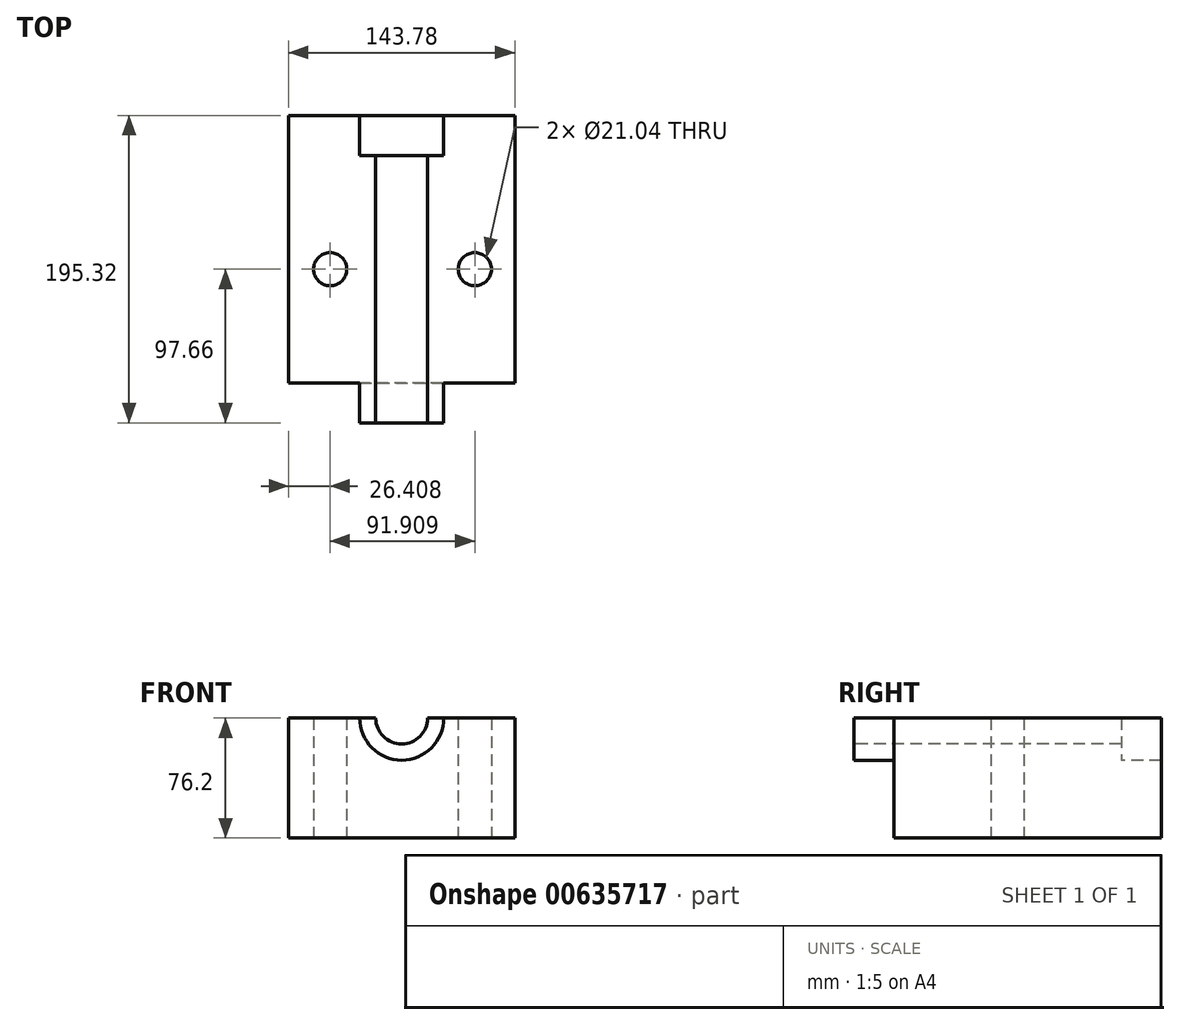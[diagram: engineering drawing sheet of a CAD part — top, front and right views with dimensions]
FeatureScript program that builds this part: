
annotation { "Feature Type Name" : "Feature", "Feature Type Description" : "" }
export const myFeature = defineFeature(function(context is Context, id is Id, definition is map)
    precondition{}
    {
        {
            var Q0;
            Q0=qCreatedBy(makeId("Top.planeOp"),FACE);
            var sketch = newSketch(context, id + "F0", { "sketchPlane" : qUnion([Q0])});
            skLineSegment(sketch, "E0.bottom", {"start": v(71.9, -72.26) * mm, "end": v(-71.9, -72.26) * mm});
            skLineSegment(sketch, "E0.top", {"start": v(71.9, 72.26) * mm, "end": v(-71.9, 72.26) * mm});
            skLineSegment(sketch, "E0.left", {"start": v(71.9, -72.26) * mm, "end": v(71.9, 72.26) * mm});
            skLineSegment(sketch, "E0.right", {"start": v(-71.9, -72.26) * mm, "end": v(-71.9, 72.26) * mm});
            skPoint(sketch, "E0.middle", {"position": v(0, 0) * mm});
            skSolve(sketch);
        }
        {
            var Q0;
            Q0=makeQuery(id+"F0.imprint","IMPRINT",FACE,{"disambiguationData":[TD([[makeQuery(id+"F0.imprint","IMPRINT",EDGE,{"derivedFrom":sQuery(id+"F0.wireOp",EDGE,"E0.bottom")}),-1.0]])]});
            extrude(context, id + "F1", {"entities" : qUnion([Q0]), "depth" : 76.2 * mm, "offsetDistance" : 25.4 * mm});
        }
        {
            var Q0;
            Q0=makeQuery(id+"F1.opExtrude","SWEPT_FACE",FACE,{"disambiguationData":[OSD([sQuery(id+"F0.wireOp",EDGE,"E0.bottom")])]});
            var sketch = newSketch(context, id + "F2", { "sketchPlane" : qUnion([Q0])});
            skArc(sketch, "E1", {"start": v(29.68, 76.2) * mm, "mid": v(0, 46.52) * mm, "end": v(-29.68, 76.2) * mm});
            skArc(sketch, "E2", {"start": v(-16.48, 76.2) * mm, "mid": v(0, 59.72) * mm, "end": v(16.48, 76.2) * mm});
            skSolve(sketch);
        }
        {
            var Q0;
            {var subQ0=sQuery(id+"F2.wireOp",EDGE,"E2");Q0=makeQuery(id+"F2.imprint","IMPRINT",FACE,{"disambiguationData":[TD([[makeQuery(id+"F2.imprint","IMPRINT",EDGE,{"derivedFrom":subQ0}),1.0]])]});}
            extrude(context, id + "F3", {"entities" : qUnion([Q0]), "operationType" : NewBodyOperationType.REMOVE, "endBound" : BoundingType.THROUGH_ALL, "oppositeDirection" : true, "depth" : 25.4 * mm, "offsetDistance" : 25.4 * mm});
        }
        {
            var Q0;
            Q0=makeQuery(id+"F1.opExtrude","SWEPT_FACE",FACE,{"disambiguationData":[OSD([sQuery(id+"F0.wireOp",EDGE,"E0.bottom")])]});
            var sketch = newSketch(context, id + "F4", { "sketchPlane" : qUnion([Q0])});
            skArc(sketch, "E3", {"start": v(-26.7, 76.2) * mm, "mid": v(0, 49.5) * mm, "end": v(26.7, 76.2) * mm});
            skSolve(sketch);
        }
        {
            var Q0;
            {var subQ0=sQuery(id+"F4.wireOp",EDGE,"E3");Q0=makeQuery(id+"F4.imprint","IMPRINT",FACE,{"disambiguationData":[TD([[makeQuery(id+"F4.imprint","IMPRINT",EDGE,{"derivedFrom":subQ0}),1.0]])]});}
            extrude(context, id + "F5", {"entities" : qUnion([Q0]), "operationType" : NewBodyOperationType.ADD, "depth" : 25.4 * mm, "offsetDistance" : 25.4 * mm});
        }
        {
            var Q0;
            Q0=makeQuery(id+"F1.opExtrude","SWEPT_FACE",FACE,{"disambiguationData":[OSD([sQuery(id+"F0.wireOp",EDGE,"E0.top")])]});
            var sketch = newSketch(context, id + "F6", { "sketchPlane" : qUnion([Q0])});
            skArc(sketch, "E4", {"start": v(26.7, 76.2) * mm, "mid": v(0, 49.5) * mm, "end": v(-26.7, 76.2) * mm});
            skSolve(sketch);
        }
        {
            var Q0;
            Q0 = qSketchRegion(id + "F6", true);
            var Q1;
            {var subQ0=sQuery(id+"F6.wireOp",EDGE,"E4");Q1=makeQuery(id+"F6.imprint","IMPRINT",FACE,{"disambiguationData":[TD([[makeQuery(id+"F6.imprint","IMPRINT",EDGE,{"derivedFrom":subQ0}),-1.0]])]});}
            extrude(context, id + "F7", {"entities" : qUnion([Q0, Q1]), "operationType" : NewBodyOperationType.ADD, "depth" : 25.4 * mm, "offsetDistance" : 25.4 * mm});
        }
        {
            var Q0;
            Q0=qCreatedBy(makeId("Top.planeOp"),FACE);
            var sketch = newSketch(context, id + "F8", { "sketchPlane" : qUnion([Q0])});
            skCircle(sketch, "E5", {"center": v(-45.48, 0) * mm, "radius": 10.52 * mm});
            skCircle(sketch, "E6", {"center": v(46.43, 0) * mm, "radius": 10.52 * mm});
            skSolve(sketch);
        }
        {
            var Q0;
            Q0=makeQuery(id+"F8.imprint","IMPRINT",FACE,{"disambiguationData":[TD([[makeQuery(id+"F8.imprint","IMPRINT",EDGE,{"derivedFrom":sQuery(id+"F8.wireOp",EDGE,"E6")}),1.0]])]});
            var Q1;
            Q1=makeQuery(id+"F8.imprint","IMPRINT",FACE,{"disambiguationData":[TD([[makeQuery(id+"F8.imprint","IMPRINT",EDGE,{"derivedFrom":sQuery(id+"F8.wireOp",EDGE,"E5")}),1.0]])]});
            extrude(context, id + "F9", {"entities" : qUnion([Q0, Q1]), "operationType" : NewBodyOperationType.REMOVE, "depth" : 101.6 * mm, "offsetDistance" : 25.4 * mm});
        }
    });
